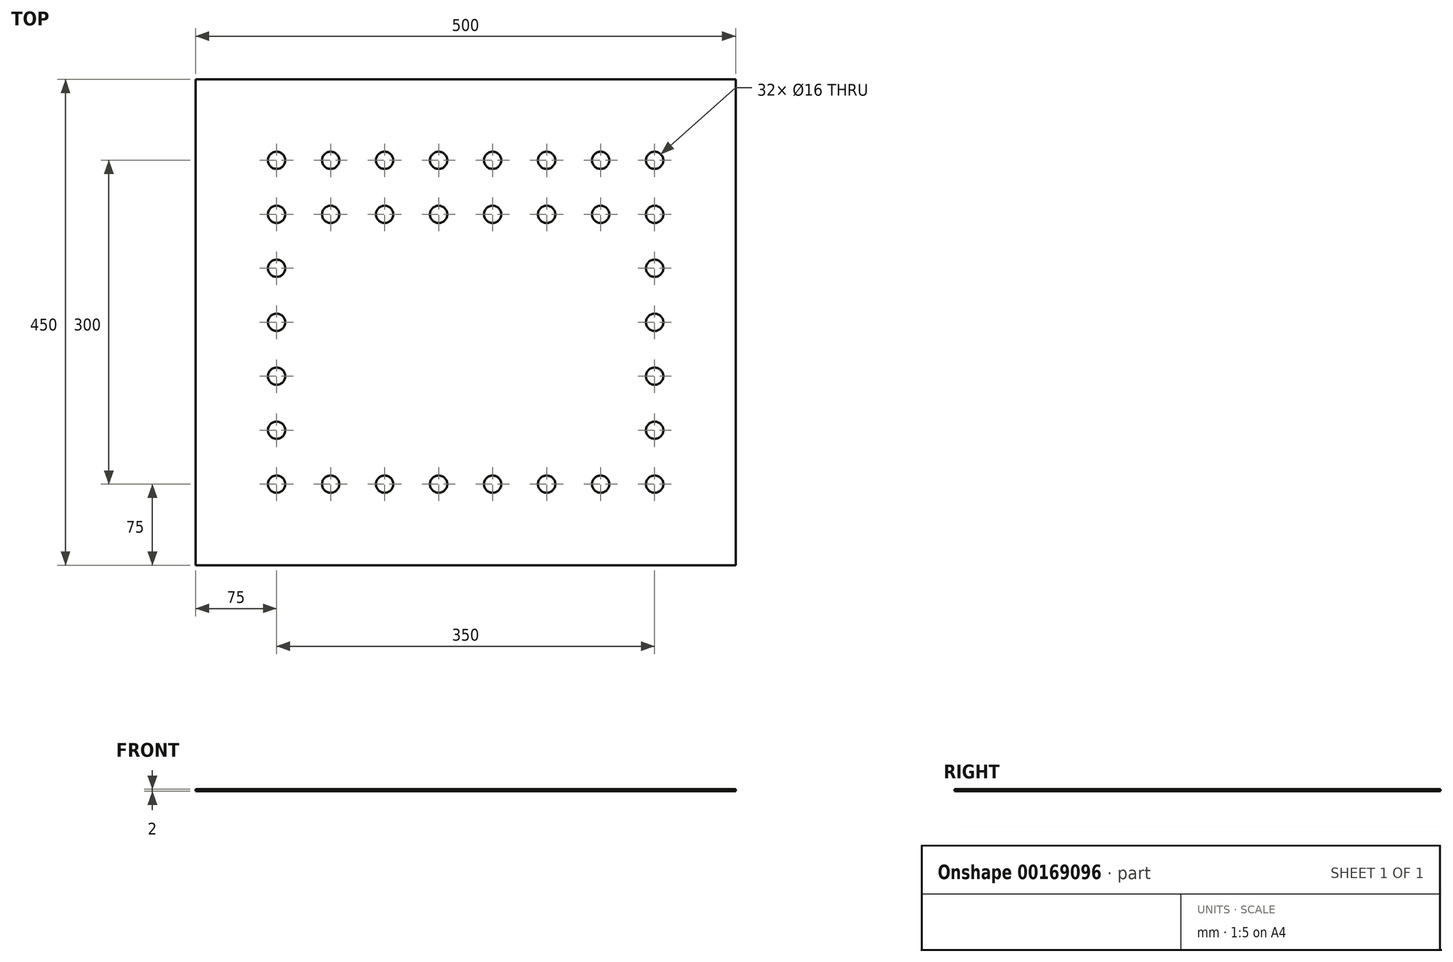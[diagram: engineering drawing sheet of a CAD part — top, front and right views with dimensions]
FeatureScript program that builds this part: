
annotation { "Feature Type Name" : "Feature", "Feature Type Description" : "" }
export const myFeature = defineFeature(function(context is Context, id is Id, definition is map)
    precondition{}
    {
        {
            var Q0;
            Q0=qCreatedBy(makeId("Top.planeOp"),FACE);
            var sketch = newSketch(context, id + "F0", { "sketchPlane" : qUnion([Q0])});
            skLineSegment(sketch, "E0.bottom", {"start": v(250, 225) * mm, "end": v(-250, 225) * mm});
            skLineSegment(sketch, "E0.top", {"start": v(250, -225) * mm, "end": v(-250, -225) * mm});
            skLineSegment(sketch, "E0.left", {"start": v(250, 225) * mm, "end": v(250, -225) * mm});
            skLineSegment(sketch, "E0.right", {"start": v(-250, 225) * mm, "end": v(-250, -225) * mm});
            skPoint(sketch, "E0.middle", {"position": v(0, 0) * mm});
            skLineSegment(sketch, "E1.bottom", {"start": v(175, 150) * mm, "end": v(-175, 150) * mm, "construction": true});
            skLineSegment(sketch, "E1.top", {"start": v(175, -150) * mm, "end": v(-175, -150) * mm, "construction": true});
            skLineSegment(sketch, "E1.left", {"start": v(175, 150) * mm, "end": v(175, -150) * mm, "construction": true});
            skLineSegment(sketch, "E1.right", {"start": v(-175, 150) * mm, "end": v(-175, -150) * mm, "construction": true});
            skCircle(sketch, "E2", {"center": v(-175, 150) * mm, "radius": 8 * mm});
            skLineSegment(sketch, "E3.1.0.0", {"start": v(225, 150) * mm, "end": v(-125, 150) * mm, "construction": true});
            skCircle(sketch, "E3.1.0.1", {"center": v(-125, 150) * mm, "radius": 8 * mm});
            skLineSegment(sketch, "E3.2.0.0", {"start": v(275, 150) * mm, "end": v(-75, 150) * mm, "construction": true});
            skCircle(sketch, "E3.2.0.1", {"center": v(-75, 150) * mm, "radius": 8 * mm});
            skLineSegment(sketch, "E3.3.0.0", {"start": v(325, 150) * mm, "end": v(-25, 150) * mm, "construction": true});
            skCircle(sketch, "E3.3.0.1", {"center": v(-25, 150) * mm, "radius": 8 * mm});
            skLineSegment(sketch, "E3.4.0.0", {"start": v(375, 150) * mm, "end": v(25, 150) * mm, "construction": true});
            skCircle(sketch, "E3.4.0.1", {"center": v(25, 150) * mm, "radius": 8 * mm});
            skLineSegment(sketch, "E3.5.0.0", {"start": v(425, 150) * mm, "end": v(75, 150) * mm, "construction": true});
            skCircle(sketch, "E3.5.0.1", {"center": v(75, 150) * mm, "radius": 8 * mm});
            skLineSegment(sketch, "E3.6.0.0", {"start": v(475, 150) * mm, "end": v(125, 150) * mm, "construction": true});
            skCircle(sketch, "E3.6.0.1", {"center": v(125, 150) * mm, "radius": 8 * mm});
            skLineSegment(sketch, "E3.7.0.0", {"start": v(525, 150) * mm, "end": v(175, 150) * mm, "construction": true});
            skCircle(sketch, "E3.7.0.1", {"center": v(175, 150) * mm, "radius": 8 * mm});
            skLineSegment(sketch, "E3.direction1", {"start": v(-175, 150) * mm, "end": v(-125, 150) * mm, "construction": true});
            skLineSegment(sketch, "E4", {"start": v(0, 0) * mm, "end": v(325.44, 0) * mm, "construction": true});
            skLineSegment(sketch, "E5.MirrorCS", {"start": v(525, -150) * mm, "end": v(175, -150) * mm, "construction": true});
            skLineSegment(sketch, "E6.MirrorCS", {"start": v(475, -150) * mm, "end": v(125, -150) * mm, "construction": true});
            skLineSegment(sketch, "E7.MirrorCS", {"start": v(325, -150) * mm, "end": v(-25, -150) * mm, "construction": true});
            skLineSegment(sketch, "E8.MirrorCS", {"start": v(425, -150) * mm, "end": v(75, -150) * mm, "construction": true});
            skLineSegment(sketch, "E9.MirrorCS", {"start": v(375, -150) * mm, "end": v(25, -150) * mm, "construction": true});
            skCircle(sketch, "E10.MirrorC", {"center": v(25, -150) * mm, "radius": 8 * mm});
            skCircle(sketch, "E11.MirrorC", {"center": v(-25, -150) * mm, "radius": 8 * mm});
            skLineSegment(sketch, "E12.MirrorCS", {"start": v(250, -225) * mm, "end": v(250, 225) * mm});
            skLineSegment(sketch, "E13.MirrorCS", {"start": v(-250, -225) * mm, "end": v(-250, 225) * mm});
            skCircle(sketch, "E14.MirrorC", {"center": v(125, -150) * mm, "radius": 8 * mm});
            skLineSegment(sketch, "E15.MirrorCS", {"start": v(-175, -150) * mm, "end": v(-125, -150) * mm, "construction": true});
            skCircle(sketch, "E16.MirrorC", {"center": v(-75, -150) * mm, "radius": 8 * mm});
            skLineSegment(sketch, "E17.MirrorCS", {"start": v(-175, -150) * mm, "end": v(-175, 150) * mm, "construction": true});
            skCircle(sketch, "E18.MirrorC", {"center": v(175, -150) * mm, "radius": 8 * mm});
            skCircle(sketch, "E19.MirrorC", {"center": v(-175, -150) * mm, "radius": 8 * mm});
            skLineSegment(sketch, "E20.MirrorCS", {"start": v(175, -150) * mm, "end": v(175, 150) * mm, "construction": true});
            skLineSegment(sketch, "E21.MirrorCS", {"start": v(225, -150) * mm, "end": v(-125, -150) * mm, "construction": true});
            skCircle(sketch, "E22.MirrorC", {"center": v(75, -150) * mm, "radius": 8 * mm});
            skLineSegment(sketch, "E23.MirrorCS", {"start": v(275, -150) * mm, "end": v(-75, -150) * mm, "construction": true});
            skCircle(sketch, "E24.MirrorC", {"center": v(-125, -150) * mm, "radius": 8 * mm});
            skCircle(sketch, "E25.0.1.0", {"center": v(175, -100) * mm, "radius": 8 * mm});
            skCircle(sketch, "E25.0.2.0", {"center": v(175, -50) * mm, "radius": 8 * mm});
            skCircle(sketch, "E25.0.3.0", {"center": v(175, 0) * mm, "radius": 8 * mm});
            skCircle(sketch, "E25.0.4.0", {"center": v(175, 50) * mm, "radius": 8 * mm});
            skCircle(sketch, "E25.0.5.0", {"center": v(175, 100) * mm, "radius": 8 * mm});
            skLineSegment(sketch, "E25.direction1", {"start": v(175, -150) * mm, "end": v(200, -150) * mm, "construction": true});
            skLineSegment(sketch, "E25.direction2", {"start": v(175, -150) * mm, "end": v(175, -100) * mm, "construction": true});
            skLineSegment(sketch, "E26", {"start": v(0, 0) * mm, "end": v(0, 91.67) * mm, "construction": true});
            skLineSegment(sketch, "E27.MirrorCS", {"start": v(-175, -150) * mm, "end": v(-175, -100) * mm, "construction": true});
            skCircle(sketch, "E28.MirrorC", {"center": v(-175, 50) * mm, "radius": 8 * mm});
            skCircle(sketch, "E29.MirrorC", {"center": v(-175, 100) * mm, "radius": 8 * mm});
            skCircle(sketch, "E30.MirrorC", {"center": v(-175, -100) * mm, "radius": 8 * mm});
            skCircle(sketch, "E31.MirrorC", {"center": v(-175, 0) * mm, "radius": 8 * mm});
            skLineSegment(sketch, "E32.MirrorCS", {"start": v(0, 0) * mm, "end": v(-325.44, 0) * mm, "construction": true});
            skCircle(sketch, "E33.MirrorC", {"center": v(-175, -50) * mm, "radius": 8 * mm});
            skCircle(sketch, "E34.1.0.0", {"center": v(-125, 100) * mm, "radius": 8 * mm});
            skCircle(sketch, "E34.2.0.0", {"center": v(-75, 100) * mm, "radius": 8 * mm});
            skCircle(sketch, "E34.3.0.0", {"center": v(-25, 100) * mm, "radius": 8 * mm});
            skCircle(sketch, "E34.4.0.0", {"center": v(25, 100) * mm, "radius": 8 * mm});
            skCircle(sketch, "E34.5.0.0", {"center": v(75, 100) * mm, "radius": 8 * mm});
            skCircle(sketch, "E34.6.0.0", {"center": v(125, 100) * mm, "radius": 8 * mm});
            skLineSegment(sketch, "E34.direction1", {"start": v(-175, 100) * mm, "end": v(-125, 100) * mm, "construction": true});
            skSolve(sketch);
        }
        {
            var Q0;
            Q0 = qSketchRegion(id + "F0", true);
            extrude(context, id + "F1", {"entities" : qUnion([Q0]), "depth" : 2 * mm});
        }
    });
